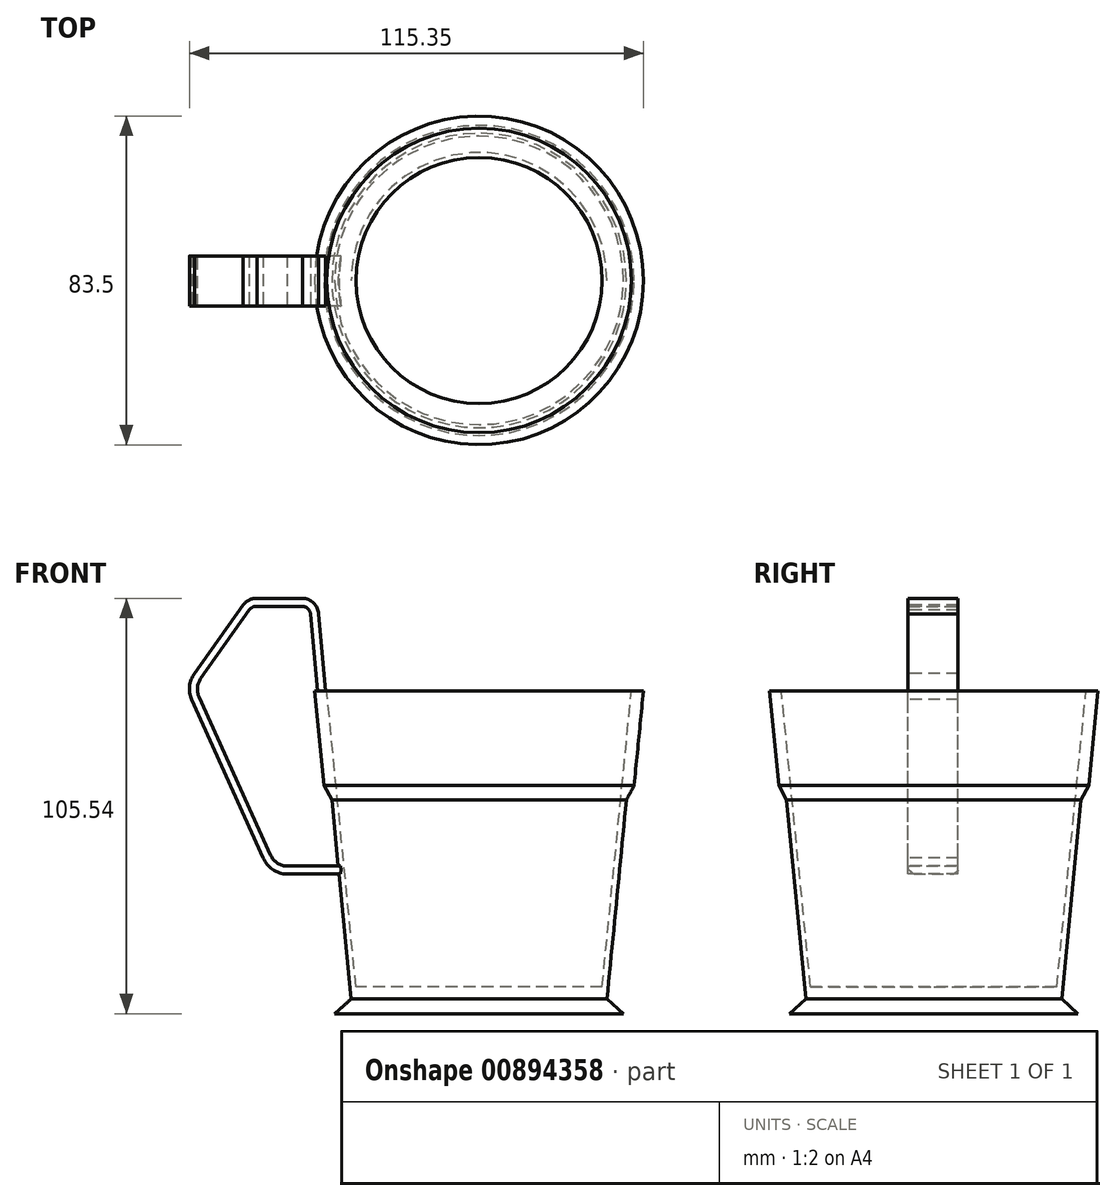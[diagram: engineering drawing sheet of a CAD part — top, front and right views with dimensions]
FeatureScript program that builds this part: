
annotation { "Feature Type Name" : "Feature", "Feature Type Description" : "" }
export const myFeature = defineFeature(function(context is Context, id is Id, definition is map)
    precondition{}
    {
        {
            var Q0;
            Q0=qCreatedBy(makeId("Top.planeOp"),FACE);
            var sketch = newSketch(context, id + "F0", { "sketchPlane" : qUnion([Q0])});
            skCircle(sketch, "E0", {"center": v(0, 0) * mm, "radius": 33.02 * mm});
            skSolve(sketch);
        }
        {
            var Q0;
            Q0=makeQuery(id+"F0.imprint","IMPRINT",FACE,{"disambiguationData":[TD([[makeQuery(id+"F0.imprint","IMPRINT",EDGE,{"derivedFrom":sQuery(id+"F0.wireOp",EDGE,"E0")}),1.0]])]});
            extrude(context, id + "F1", {"entities" : qUnion([Q0]), "depth" : 78.23 * mm, "offsetDistance" : 25.4 * mm, "hasDraft" : true, "draftAngle" : 5.63 * degree});
        }
        {
            var Q0;
            Q0=qCreatedBy(makeId("Front.planeOp"),FACE);
            var sketch = newSketch(context, id + "F2", { "sketchPlane" : qUnion([Q0])});
            skLineSegment(sketch, "E1", {"start": v(0, 0) * mm, "end": v(-32.51, 0) * mm});
            skLineSegment(sketch, "E2", {"start": v(-36.65, -3.7) * mm, "end": v(0, -3.7) * mm});
            skLineSegment(sketch, "E3", {"start": v(0, -3.7) * mm, "end": v(0, 0) * mm});
            skLineSegment(sketch, "E4", {"start": v(-32.51, 0) * mm, "end": v(-36.65, -3.7) * mm});
            skSolve(sketch);
        }
        {
            var Q0;
            Q0=makeQuery(id+"F1.opExtrude","CAP_FACE",FACE,{"disambiguationData":[OSD([sQuery(id+"F0.wireOp",EDGE,"E0")])],"isStart":true});
            var sketch = newSketch(context, id + "F3", { "sketchPlane" : qUnion([Q0])});
            skCircle(sketch, "E5", {"center": v(0, 0) * mm, "radius": 34.04 * mm});
            skSolve(sketch);
        }
        {
            var Q0;
            Q0=makeQuery(id+"F3.imprint","IMPRINT",FACE,{"disambiguationData":[TD([[makeQuery(id+"F3.imprint","IMPRINT",EDGE,{"derivedFrom":sQuery(id+"F3.wireOp",EDGE,"E5")}),1.0]])]});
            extrude(context, id + "F4", {"entities" : qUnion([Q0]), "operationType" : NewBodyOperationType.ADD, "oppositeDirection" : true, "depth" : 78.23 * mm, "offsetDistance" : 25.4 * mm, "hasDraft" : true, "draftAngle" : 5.63 * degree});
        }
        {
            var Q0;
            {var subQ0=sQuery(id+"F0.wireOp",EDGE,"E0");Q0=makeQuery(id+"F4.boolean.opBoolean","MERGE",FACE,{"derivedFrom":[makeQuery(id+"F1.opExtrude","CAP_FACE",FACE,{"disambiguationData":[OSD([subQ0])],"isStart":false}),makeQuery(id+"F4.opExtrude","CAP_FACE",FACE,{"disambiguationData":[OSD([subQ0,sQuery(id+"F3.wireOp",EDGE,"E5")])],"isStart":false})]});}
            shell(context, id + "F5", {"entities" : qUnion([Q0]), "thickness" : 3.05 * mm});
        }
        {
            var Q0;
            Q0=qCreatedBy(makeId("Front.planeOp"),FACE);
            var sketch = newSketch(context, id + "F6", { "sketchPlane" : qUnion([Q0])});
            skLineSegment(sketch, "E6", {"start": v(32.5, 0) * mm, "end": v(37.4, 50.54) * mm});
            skLineSegment(sketch, "E7", {"start": v(44.09, 0) * mm, "end": v(32.5, 0) * mm});
            skLineSegment(sketch, "E8", {"start": v(0, 0) * mm, "end": v(0, 77.76) * mm});
            skLineSegment(sketch, "E9", {"start": v(44.09, 54.35) * mm, "end": v(39.45, 54.35) * mm});
            skLineSegment(sketch, "E10", {"start": v(39.45, 54.35) * mm, "end": v(37.4, 50.54) * mm});
            skLineSegment(sketch, "E11", {"start": v(44.09, 54.35) * mm, "end": v(44.09, 0) * mm});
            skPoint(sketch, "E12.orphan", {"position": v(50.5, 0) * mm});
            skSolve(sketch);
        }
        {
            var Q0;
            Q0=makeQuery(id+"F6.imprint","IMPRINT",FACE,{"disambiguationData":[TD([[makeQuery(id+"F6.imprint","IMPRINT",EDGE,{"derivedFrom":sQuery(id+"F6.wireOp",EDGE,"E6")}),-1.0]])]});
            var Q1;
            Q1=sQuery(id+"F6.wireOp",EDGE,"E8");
            revolve(context, id + "F7", {"operationType" : NewBodyOperationType.REMOVE, "surfaceOperationType" : NewSurfaceOperationType.NEW, "entities" : qUnion([Q0]), "axis" : qUnion([Q1]), "revolveType" : RevolveType.FULL, "oppositeDirection" : true});
        }
        {
            var Q0;
            Q0=qCreatedBy(makeId("Front.planeOp"),FACE);
            var sketch = newSketch(context, id + "F8", { "sketchPlane" : qUnion([Q0])});
            skLineSegment(sketch, "E13", {"start": v(-40.63, 77.71) * mm, "end": v(-42.46, 97.85) * mm});
            skLineSegment(sketch, "E14", {"start": v(-71.47, 76.61) * mm, "end": v(-53.27, 36.42) * mm});
            skLineSegment(sketch, "E15", {"start": v(-48.64, 33.43) * mm, "end": v(-35.06, 33.43) * mm});
            skPoint(sketch, "E16.visualSharp", {"position": v(-40.94, 105.2) * mm});
            skPoint(sketch, "E17.visualSharp", {"position": v(-78.7, 92.55) * mm});
            skPoint(sketch, "E18.visualSharp", {"position": v(-51.92, 33.43) * mm});
            skArc(sketch, "E18.filletArc", {"start": v(-53.27, 36.42) * mm, "mid": v(-51.4, 34.24) * mm, "end": v(-48.64, 33.43) * mm});
            skLineSegment(sketch, "E19", {"start": v(-45, 100.16) * mm, "end": v(-56.57, 100.16) * mm});
            skLineSegment(sketch, "E20", {"start": v(-58.64, 99.09) * mm, "end": v(-71, 81.64) * mm});
            skPoint(sketch, "E21.visualSharp", {"position": v(-72.67, 79.26) * mm});
            skArc(sketch, "E21.filletArc", {"start": v(-71, 81.64) * mm, "mid": v(-71.9, 79.2) * mm, "end": v(-71.47, 76.61) * mm});
            skPoint(sketch, "E22.visualSharp", {"position": v(-57.88, 100.16) * mm});
            skArc(sketch, "E22.filletArc", {"start": v(-56.57, 100.16) * mm, "mid": v(-57.74, 99.88) * mm, "end": v(-58.64, 99.09) * mm});
            skPoint(sketch, "E23.visualSharp", {"position": v(-42.67, 100.16) * mm});
            skArc(sketch, "E23.filletArc", {"start": v(-42.46, 97.85) * mm, "mid": v(-43.28, 99.5) * mm, "end": v(-45, 100.16) * mm});
            skSolve(sketch);
        }
        {
            var Q0;
            {var subQ0=sQuery(id+"F0.wireOp",EDGE,"E0");Q0=makeQuery(id+"F4.boolean.opBoolean","MERGE",FACE,{"derivedFrom":[makeQuery(id+"F1.opExtrude","CAP_FACE",FACE,{"disambiguationData":[OSD([subQ0])],"isStart":false}),makeQuery(id+"F4.opExtrude","CAP_FACE",FACE,{"disambiguationData":[OSD([subQ0,sQuery(id+"F3.wireOp",EDGE,"E5")])],"isStart":false})]});}
            var sketch = newSketch(context, id + "F9", { "sketchPlane" : qUnion([Q0])});
            skLineSegment(sketch, "E24.bottom", {"start": v(-73.58, 6.2) * mm, "end": v(-71.55, 6.2) * mm});
            skLineSegment(sketch, "E24.top", {"start": v(-73.58, -6.5) * mm, "end": v(-71.55, -6.5) * mm});
            skLineSegment(sketch, "E24.left", {"start": v(-73.58, 6.2) * mm, "end": v(-73.58, -6.5) * mm});
            skLineSegment(sketch, "E24.right", {"start": v(-71.55, 6.2) * mm, "end": v(-71.55, -6.5) * mm});
            skSolve(sketch);
        }
        {
            var Q0;
            Q0=makeQuery(id+"F2.imprint","IMPRINT",FACE,{"disambiguationData":[TD([[makeQuery(id+"F2.imprint","IMPRINT",EDGE,{"derivedFrom":sQuery(id+"F2.wireOp",EDGE,"E1")}),1.0]])]});
            var Q1;
            Q1=sQuery(id+"F2.wireOp",EDGE,"E3");
            revolve(context, id + "F10", {"operationType" : NewBodyOperationType.ADD, "surfaceOperationType" : NewSurfaceOperationType.NEW, "entities" : qUnion([Q0]), "axis" : qUnion([Q1]), "revolveType" : RevolveType.FULL});
        }
        {
            var Q0;
            Q0=makeQuery(id+"F9.imprint","IMPRINT",FACE,{"disambiguationData":[TD([[makeQuery(id+"F9.imprint","IMPRINT",EDGE,{"derivedFrom":sQuery(id+"F9.wireOp",EDGE,"E24.bottom")}),-1.0]])]});
            var Q1;
            Q1=sQuery(id+"F8.wireOp",EDGE,"E21.filletArc");
            var Q2;
            Q2=sQuery(id+"F8.wireOp",EDGE,"E20");
            var Q3;
            Q3=sQuery(id+"F8.wireOp",EDGE,"E22.filletArc");
            var Q4;
            Q4=sQuery(id+"F8.wireOp",EDGE,"E19");
            var Q5;
            Q5=sQuery(id+"F8.wireOp",EDGE,"E23.filletArc");
            var Q6;
            Q6=sQuery(id+"F8.wireOp",EDGE,"E13");
            var Q7;
            Q7=sQuery(id+"F8.wireOp",EDGE,"E14");
            var Q8;
            Q8=sQuery(id+"F8.wireOp",EDGE,"E18.filletArc");
            var Q9;
            Q9=sQuery(id+"F8.wireOp",EDGE,"E15");
            sweep(context, id + "F11", {"operationType" : NewBodyOperationType.ADD, "profiles" : qUnion([Q0]), "path" : qUnion([Q1, Q2, Q3, Q4, Q5, Q6, Q7, Q8, Q9])});
        }
    });
